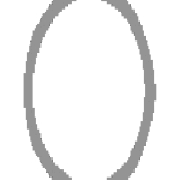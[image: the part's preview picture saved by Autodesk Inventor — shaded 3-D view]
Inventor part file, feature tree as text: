
AUTODESK INVENTOR PART (.ipt)
format: ipt  version: 2021 (Build 250183000, 183)  size: 109,568 bytes
history: native  units: in
note: dims shown in document units (in); Inventor stores cm internally (conversion verified against a paired STEP export)
features: other x4, sketch x3, plane x1
ambient origin geometry x8: Origin, YZ Plane, XZ Plane, XY Plane, X Axis, Y Axis, Z Axis, Center Point
bodies: Solid1 (feature_tree), Body (feature_tree)
feature tree (8):
  other  "Driven Length"
  other  "Frame Generator"
  other  "Start Plane"
  other  "End Plane"
  sketch  "Sketch"  dims[d2=22.0in d4=-0.0in d5=22.0in d6=0.12in d7=0.0in d8=90.0deg d9=22.0in]
  sketch  "Sketch2"  dims[d0=1.0in]
  plane  "Work Plane3"
  sketch  "Sketch3"  dims[d1=0.065in]
